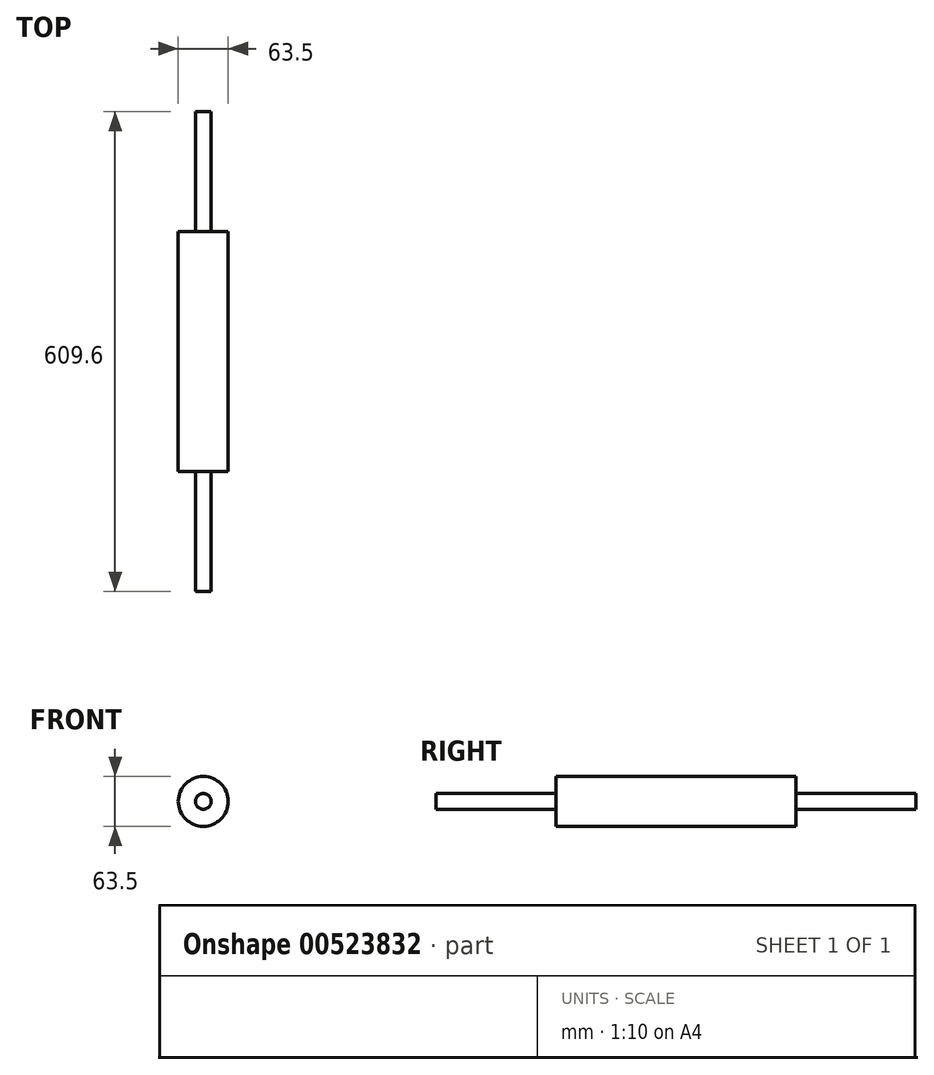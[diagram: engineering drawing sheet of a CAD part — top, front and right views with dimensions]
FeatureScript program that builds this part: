
annotation { "Feature Type Name" : "Feature", "Feature Type Description" : "" }
export const myFeature = defineFeature(function(context is Context, id is Id, definition is map)
    precondition{}
    {
        {
            var Q0;
            Q0=qCreatedBy(makeId("Front.planeOp"),FACE);
            var sketch = newSketch(context, id + "F0", { "sketchPlane" : qUnion([Q0])});
            skCircle(sketch, "E0", {"center": v(0, 0) * mm, "radius": 31.75 * mm});
            skCircle(sketch, "E1", {"center": v(0, 0) * mm, "radius": 10 * mm});
            skSolve(sketch);
        }
        {
            var Q0;
            Q0=makeQuery(id+"F0.imprint","IMPRINT",FACE,{"disambiguationData":[TD([[makeQuery(id+"F0.imprint","IMPRINT",EDGE,{"derivedFrom":sQuery(id+"F0.wireOp",EDGE,"E0")}),1.0]])]});
            var Q1;
            Q1=makeQuery(id+"F0.imprint","IMPRINT",FACE,{"disambiguationData":[TD([[makeQuery(id+"F0.imprint","IMPRINT",EDGE,{"derivedFrom":sQuery(id+"F0.wireOp",EDGE,"E1")}),1.0]])]});
            extrude(context, id + "F1", {"entities" : qUnion([Q0, Q1]), "oppositeDirection" : true, "depth" : 304.8 * mm, "offsetDistance" : 25.4 * mm});
        }
        {
            var Q0;
            Q0=makeQuery(id+"F0.imprint","IMPRINT",FACE,{"disambiguationData":[TD([[makeQuery(id+"F0.imprint","IMPRINT",EDGE,{"derivedFrom":sQuery(id+"F0.wireOp",EDGE,"E1")}),1.0]])]});
            extrude(context, id + "F2", {"entities" : qUnion([Q0]), "operationType" : NewBodyOperationType.ADD, "depth" : 152.4 * mm, "offsetDistance" : 25.4 * mm});
        }
        {
            var Q0;
            Q0=makeQuery(id+"F2.opExtrude","CAP_FACE",FACE,{"disambiguationData":[OSD([sQuery(id+"F0.wireOp",EDGE,"E1")])],"isStart":false});
            extrude(context, id + "F3", {"entities" : qUnion([Q0]), "operationType" : NewBodyOperationType.ADD, "oppositeDirection" : true, "depth" : 609.6 * mm, "offsetDistance" : 25.4 * mm});
        }
    });
